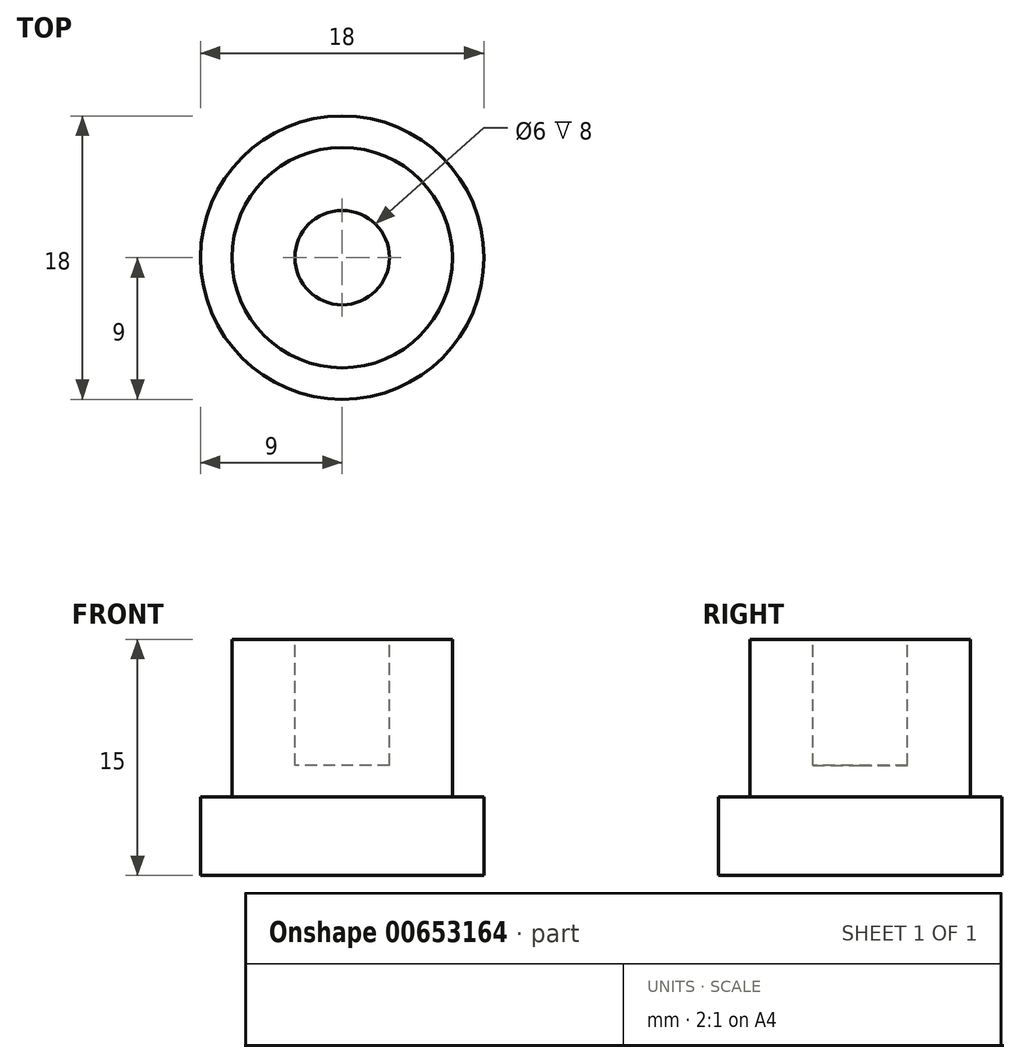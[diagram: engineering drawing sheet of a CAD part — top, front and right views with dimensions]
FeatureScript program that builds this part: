
annotation { "Feature Type Name" : "Feature", "Feature Type Description" : "" }
export const myFeature = defineFeature(function(context is Context, id is Id, definition is map)
    precondition{}
    {
        {
            var Q0;
            Q0=qCreatedBy(makeId("Top.planeOp"),FACE);
            var sketch = newSketch(context, id + "F0", { "sketchPlane" : qUnion([Q0])});
            skCircle(sketch, "E0", {"center": v(0, 0) * mm, "radius": 9 * mm});
            skCircle(sketch, "E1", {"center": v(0, 0) * mm, "radius": 7 * mm});
            skCircle(sketch, "E2", {"center": v(0, 0) * mm, "radius": 11 * mm});
            skSolve(sketch);
        }
        {
            var Q0;
            Q0=makeQuery(id+"F0.imprint","IMPRINT",FACE,{"disambiguationData":[TD([[makeQuery(id+"F0.imprint","IMPRINT",EDGE,{"derivedFrom":sQuery(id+"F0.wireOp",EDGE,"E1")}),1.0]])]});
            var Q1;
            Q1=makeQuery(id+"F0.imprint","IMPRINT",FACE,{"disambiguationData":[TD([[makeQuery(id+"F0.imprint","IMPRINT",EDGE,{"derivedFrom":sQuery(id+"F0.wireOp",EDGE,"E0")}),1.0]])]});
            extrude(context, id + "F1", {"entities" : qUnion([Q0, Q1]), "oppositeDirection" : true, "depth" : 5 * mm, "offsetDistance" : 25 * mm});
        }
        {
            var Q0;
            Q0=makeQuery(id+"F0.imprint","IMPRINT",FACE,{"disambiguationData":[TD([[makeQuery(id+"F0.imprint","IMPRINT",EDGE,{"derivedFrom":sQuery(id+"F0.wireOp",EDGE,"E1")}),1.0]])]});
            extrude(context, id + "F2", {"entities" : qUnion([Q0]), "operationType" : NewBodyOperationType.ADD, "depth" : 10 * mm, "offsetDistance" : 25 * mm});
        }
        {
            var Q0;
            Q0=makeQuery(id+"F2.opExtrude","CAP_FACE",FACE,{"disambiguationData":[OSD([sQuery(id+"F0.wireOp",EDGE,"E1")])],"isStart":false});
            var sketch = newSketch(context, id + "F3", { "sketchPlane" : qUnion([Q0])});
            skCircle(sketch, "E3", {"center": v(0, 0) * mm, "radius": 3 * mm});
            skSolve(sketch);
        }
        {
            var Q0;
            Q0=makeQuery(id+"F3.imprint","IMPRINT",FACE,{"disambiguationData":[TD([[makeQuery(id+"F3.imprint","IMPRINT",EDGE,{"derivedFrom":sQuery(id+"F3.wireOp",EDGE,"E3")}),1.0]])]});
            extrude(context, id + "F4", {"entities" : qUnion([Q0]), "operationType" : NewBodyOperationType.REMOVE, "oppositeDirection" : true, "depth" : 8 * mm, "offsetDistance" : 25 * mm});
        }
    });
